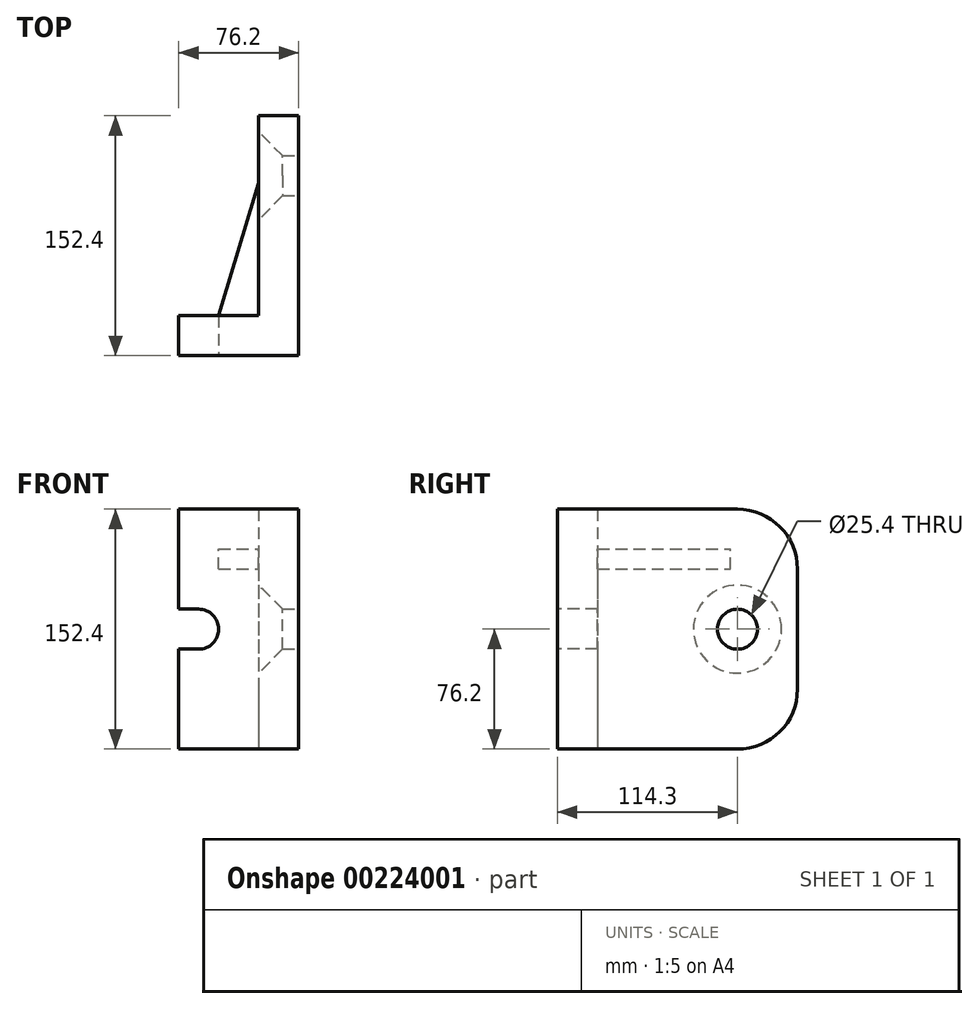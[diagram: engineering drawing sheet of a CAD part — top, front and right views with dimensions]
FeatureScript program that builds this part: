
annotation { "Feature Type Name" : "Feature", "Feature Type Description" : "" }
export const myFeature = defineFeature(function(context is Context, id is Id, definition is map)
    precondition{}
    {
        {
            var Q0;
            Q0=qCreatedBy(makeId("Top.planeOp"),FACE);
            var sketch = newSketch(context, id + "F0", { "sketchPlane" : qUnion([Q0])});
            skLineSegment(sketch, "E0", {"start": v(-76.2, 0) * mm, "end": v(-76.2, 25.4) * mm});
            skLineSegment(sketch, "E1", {"start": v(-76.2, 25.4) * mm, "end": v(-25.4, 25.4) * mm});
            skLineSegment(sketch, "E2", {"start": v(-25.4, 25.4) * mm, "end": v(-25.4, 152.4) * mm});
            skLineSegment(sketch, "E3", {"start": v(0, 152.4) * mm, "end": v(0, 0) * mm});
            skLineSegment(sketch, "E4", {"start": v(0, 0) * mm, "end": v(-76.2, 0) * mm});
            skLineSegment(sketch, "E5", {"start": v(-25.4, 152.4) * mm, "end": v(0, 152.4) * mm});
            skSolve(sketch);
        }
        {
            var Q0;
            Q0=makeQuery(id+"F0.imprint","IMPRINT",FACE,{"disambiguationData":[TD([[makeQuery(id+"F0.imprint","IMPRINT",EDGE,{"derivedFrom":sQuery(id+"F0.wireOp",EDGE,"E0")}),-1.0]])]});
            extrude(context, id + "F1", {"entities" : qUnion([Q0]), "endBound" : BoundingType.SYMMETRIC, "depth" : 152.4 * mm});
        }
        {
            var Q0;
            Q0=makeQuery(id+"F1.opExtrude","SWEPT_FACE",FACE,{"disambiguationData":[OSD([sQuery(id+"F0.wireOp",EDGE,"E3")])]});
            var sketch = newSketch(context, id + "F2", { "sketchPlane" : qUnion([Q0])});
            skCircle(sketch, "E6", {"center": v(114.3, 0) * mm, "radius": 12.7 * mm});
            skSolve(sketch);
        }
        {
            var Q0;
            Q0=makeQuery(id+"F2.imprint","IMPRINT",FACE,{"disambiguationData":[TD([[makeQuery(id+"F2.imprint","IMPRINT",EDGE,{"derivedFrom":sQuery(id+"F2.wireOp",EDGE,"E6")}),1.0]])]});
            extrude(context, id + "F3", {"entities" : qUnion([Q0]), "operationType" : NewBodyOperationType.REMOVE, "endBound" : BoundingType.THROUGH_ALL, "oppositeDirection" : true, "depth" : 25.4 * mm});
        }
        {
            var Q0;
            Q0=makeQuery(id+"F1.opExtrude","SWEPT_FACE",FACE,{"disambiguationData":[OSD([sQuery(id+"F0.wireOp",EDGE,"E4")])]});
            var sketch = newSketch(context, id + "F4", { "sketchPlane" : qUnion([Q0])});
            skLineSegment(sketch, "E7", {"start": v(-63.5, 12.7) * mm, "end": v(-76.2, 12.7) * mm});
            skLineSegment(sketch, "E8", {"start": v(-63.5, -12.7) * mm, "end": v(-76.2, -12.7) * mm});
            skArc(sketch, "E9", {"start": v(-63.5, -12.7) * mm, "mid": v(-50.8, 0) * mm, "end": v(-63.5, 12.7) * mm});
            skLineSegment(sketch, "E10", {"start": v(-76.2, 12.7) * mm, "end": v(-76.2, -12.7) * mm});
            skSolve(sketch);
        }
        {
            var Q0;
            Q0=makeQuery(id+"F4.imprint","IMPRINT",FACE,{"disambiguationData":[TD([[makeQuery(id+"F4.imprint","IMPRINT",EDGE,{"derivedFrom":sQuery(id+"F4.wireOp",EDGE,"E7")}),1.0]])]});
            extrude(context, id + "F5", {"entities" : qUnion([Q0]), "operationType" : NewBodyOperationType.REMOVE, "oppositeDirection" : true, "depth" : 25.4 * mm});
        }
        {
            var Q0;
            Q0=qCreatedBy(makeId("Top.planeOp"),FACE);
            cPlane(context, id + "F6", {"entities" : qUnion([Q0]), "cplaneType" : CPlaneType.OFFSET, "offset" : 44.45 * mm, "width" : 152.4 * mm, "height" : 152.4 * mm});
        }
        {
            var Q0;
            Q0=qCreatedBy(id+"F6.planeOp",FACE);
            var sketch = newSketch(context, id + "F7", { "sketchPlane" : qUnion([Q0])});
            skLineSegment(sketch, "E11.0", {"start": v(-25.4, 25.4) * mm, "end": v(-25.4, 152.4) * mm});
            skLineSegment(sketch, "E12.0", {"start": v(-76.2, 25.4) * mm, "end": v(-25.4, 25.4) * mm});
            skPoint(sketch, "E13.end.orphan", {"position": v(-50.8, 25.4) * mm});
            skLineSegment(sketch, "E14", {"start": v(-50.8, 25.4) * mm, "end": v(-25.4, 109.76) * mm});
            skSolve(sketch);
        }
        {
            var Q0;
            {var subQ0=sQuery(id+"F7.wireOp",EDGE,"E11.0");Q0=makeQuery(id+"F7.imprint","IMPRINT",FACE,{"disambiguationData":[TD([[makeQuery(id+"F7.imprint","IMPRINT",EDGE,{"derivedFrom":subQ0}),1.0]])]});}
            extrude(context, id + "F8", {"entities" : qUnion([Q0]), "operationType" : NewBodyOperationType.ADD, "endBound" : BoundingType.SYMMETRIC, "oppositeDirection" : true, "depth" : 12.7 * mm});
        }
        {
            var Q0;
            Q0=makeQuery(id+"F1.opExtrude","CAP_EDGE",EDGE,{"disambiguationData":[OSD([sQuery(id+"F0.wireOp",EDGE,"E5")])],"isStart":false});
            fillet(context, id + "F9", {"entities" : qUnion([Q0]), "radius" : 38.1 * mm, "tangentPropagation" : true, "allowEdgeOverflow" : false});
        }
        {
            var Q0;
            Q0=makeQuery(id+"F1.opExtrude","CAP_EDGE",EDGE,{"disambiguationData":[OSD([sQuery(id+"F0.wireOp",EDGE,"E5")])],"isStart":true});
            fillet(context, id + "F10", {"entities" : qUnion([Q0]), "radius" : 38.1 * mm, "tangentPropagation" : true, "allowEdgeOverflow" : false});
        }
        {
            var Q0;
            Q0=makeQuery(id+"F3.boolean.opBoolean","INTERSECT",EDGE,{"derivedFrom":[makeQuery(id+"F1.opExtrude","SWEPT_FACE",FACE,{"disambiguationData":[OSD([sQuery(id+"F0.wireOp",EDGE,"E2")])]}),makeQuery(id+"F3.opExtrude","SWEPT_FACE",FACE,{"disambiguationData":[OSD([sQuery(id+"F2.wireOp",EDGE,"E6")])]})]});
            chamfer(context, id + "F11", {"entities" : qUnion([Q0]), "width" : 15.24 * mm, "tangentPropagation" : true});
        }
    });
